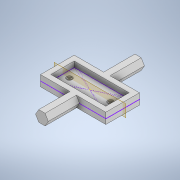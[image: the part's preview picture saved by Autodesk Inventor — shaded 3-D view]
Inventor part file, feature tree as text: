
AUTODESK INVENTOR PART (.ipt)
format: ipt  version: 2021.1 (Build 251245010, 245A)  size: 150,528 bytes
history: native  units: in
note: dims shown in document units (in); Inventor stores cm internally (conversion verified against a paired STEP export)
features: sketch x3, extrude x3, hole x1, mirror x1
ambient origin geometry x8: Origin, YZ Plane, XZ Plane, XY Plane, X Axis, Y Axis, Z Axis, Center Point
bodies: Solid1 (feature_tree)
feature tree (8):
  sketch  "Sketch1"  dims[d4=0.375in d5=0.0in]
  extrude  "Extrusion1"  TaperAngle=0.0deg  [1 undecoded]
  extrude  "Extrusion2"  Depth=0.5in
  hole  "Hole1"  [1 undecoded]
  extrude  "Extrusion5"  [1 undecoded]
  mirror  "Mirror2"
  sketch  "Sketch5"  dims[d7=0.0in d16=0.5in]
  sketch  "Sketch6"  dims[d17=0.201in d18=0.25in d19=0.4in d20=0.1in d21=0.5635in d22=0.25in d23=0.0in d25=2.275in d26=0.0in]
note: 3 required parameter values undecoded (feature->parameter linkage not recoverable at this tier; creation-order binding heuristic only, values carry confidence <= 0.55)
